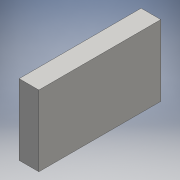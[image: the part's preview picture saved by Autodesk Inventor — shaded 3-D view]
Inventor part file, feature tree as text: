
AUTODESK INVENTOR PART (.ipt)
format: ipt  version: 2016 (Build 200138000, 138)  size: 82,432 bytes
history: native  units: mm
features: other x1, extrude x1, sketch x1
ambient origin geometry x8: Origin, YZ Plane, XZ Plane, XY Plane, X Axis, Y Axis, Z Axis, Center Point
bodies: Body1 (feature_tree)
feature tree (3):
  other  "Sólido1"
  extrude  "Extrusión1"  Depth=18.0mm
  sketch  "Boceto1"  dims[d0=31.0mm d1=18.0mm d2=5.0mm d3=0.0mm]
